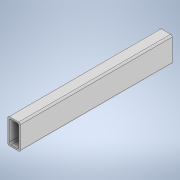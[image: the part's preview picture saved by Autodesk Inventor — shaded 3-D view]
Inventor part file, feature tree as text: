
AUTODESK INVENTOR PART (.ipt)
format: ipt  version: 2020 (Build 240168000, 168)  size: 125,440 bytes
history: native  units: in
note: dims shown in document units (in); Inventor stores cm internally (conversion verified against a paired STEP export)
features: extrude x1, sketch x1
ambient origin geometry x8: Origin, YZ Plane, XZ Plane, XY Plane, X Axis, Y Axis, Z Axis, Center Point
bodies: Solid1 (feature_tree)
feature tree (2):
  extrude  "Extrusion1"  Depth=1.0in
  sketch  "Sketch1"  dims[d0=2.0in d1=1.0in d2=0.125in d3=0.125in d4=0.125in d5=0.125in d6=0.125in d7=0.125in d8=0.125in d9=0.125in d10=0.125in d11=12.0in d12=0.0in]
